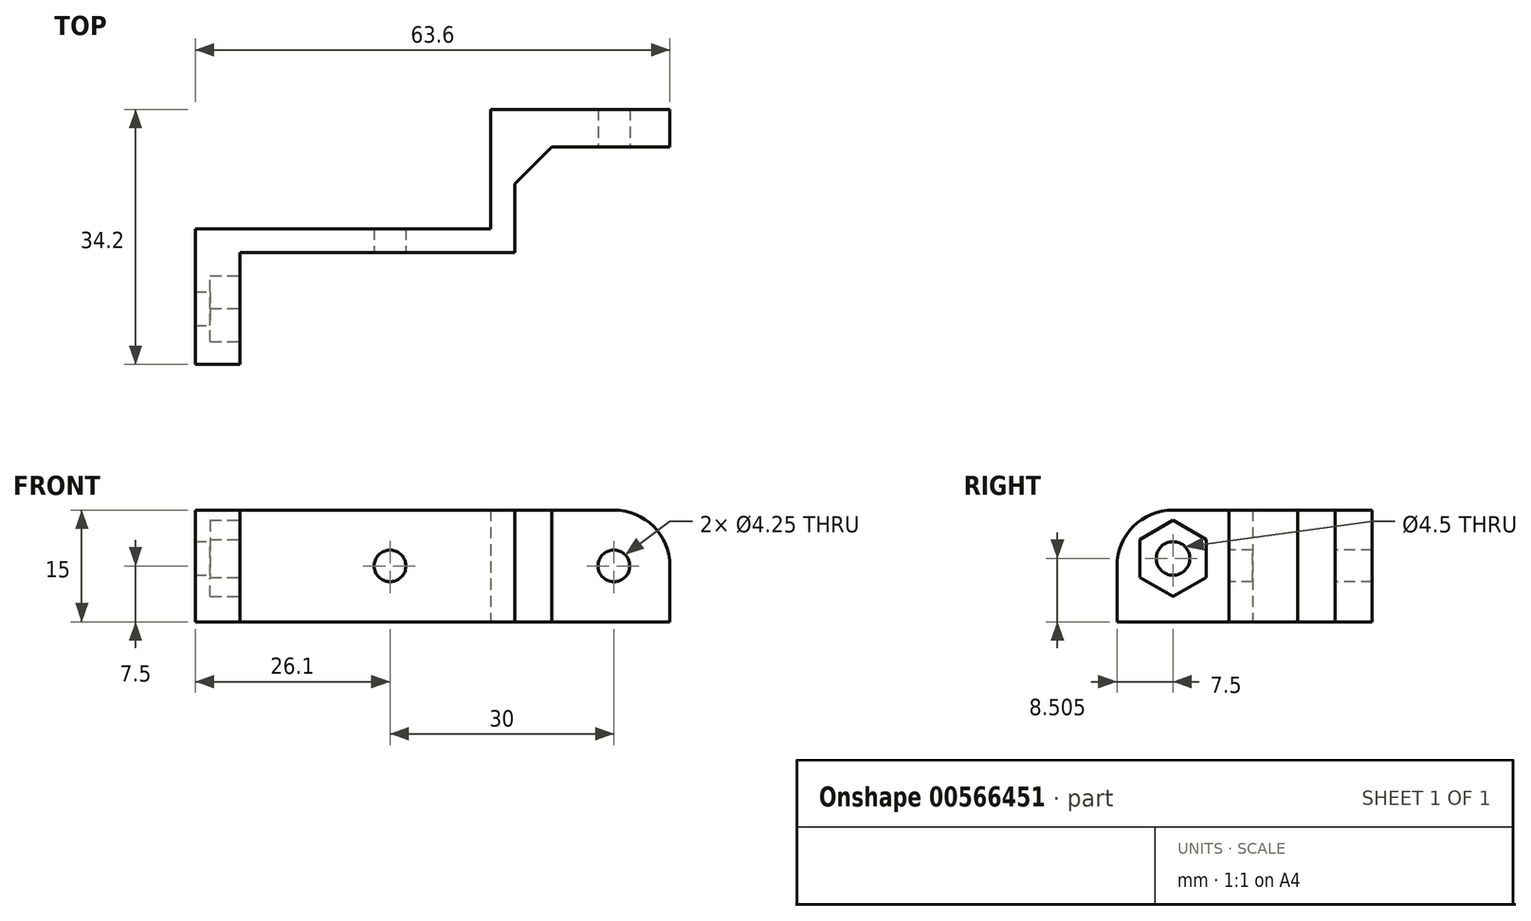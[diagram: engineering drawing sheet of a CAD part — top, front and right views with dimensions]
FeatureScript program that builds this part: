
annotation { "Feature Type Name" : "Feature", "Feature Type Description" : "" }
export const myFeature = defineFeature(function(context is Context, id is Id, definition is map)
    precondition{}
    {
        {
            var Q0;
            Q0=qCreatedBy(makeId("Top.planeOp"),FACE);
            var sketch = newSketch(context, id + "F0", { "sketchPlane" : qUnion([Q0])});
            skLineSegment(sketch, "E0", {"start": v(0, 0) * mm, "end": v(-16.7, 0) * mm});
            skLineSegment(sketch, "E1", {"start": v(-16.7, 0) * mm, "end": v(-16.7, 14.2) * mm, "construction": true});
            skLineSegment(sketch, "E2", {"start": v(-47.5, 14.2) * mm, "end": v(-47.5, 19.2) * mm, "construction": true});
            skLineSegment(sketch, "E3", {"start": v(-13.5, 19.2) * mm, "end": v(-13.5, 3.2) * mm, "construction": true});
            skLineSegment(sketch, "E4", {"start": v(-13.5, 3.2) * mm, "end": v(0, 3.2) * mm});
            skLineSegment(sketch, "E5.MirrorCS", {"start": v(47.5, 14.2) * mm, "end": v(47.5, 19.2) * mm, "construction": true});
            skLineSegment(sketch, "E6.MirrorCS", {"start": v(16.7, 14.2) * mm, "end": v(47.5, 14.2) * mm, "construction": true});
            skLineSegment(sketch, "E7.MirrorCS", {"start": v(47.5, 19.2) * mm, "end": v(13.5, 19.2) * mm, "construction": true});
            skLineSegment(sketch, "E8.MirrorCS", {"start": v(0, 0) * mm, "end": v(16.7, 0) * mm});
            skLineSegment(sketch, "E9.MirrorCS", {"start": v(13.5, 3.2) * mm, "end": v(0, 3.2) * mm});
            skLineSegment(sketch, "E10.MirrorCS", {"start": v(16.7, 0) * mm, "end": v(16.7, 14.2) * mm});
            skLineSegment(sketch, "E11.MirrorCS", {"start": v(13.5, 19.2) * mm, "end": v(13.5, 3.2) * mm});
            skLineSegment(sketch, "E12", {"start": v(13.5, 19.2) * mm, "end": v(37.5, 19.2) * mm});
            skLineSegment(sketch, "E13", {"start": v(37.5, 19.2) * mm, "end": v(37.5, 14.2) * mm});
            skLineSegment(sketch, "E14", {"start": v(37.5, 14.2) * mm, "end": v(16.7, 14.2) * mm});
            skLineSegment(sketch, "E15", {"start": v(-26.1, 3.2) * mm, "end": v(-13.5, 3.2) * mm});
            skPoint(sketch, "E16.orphan", {"position": v(-20.5, 0) * mm});
            skLineSegment(sketch, "E17", {"start": v(-26.1, 3.2) * mm, "end": v(-26.1, -15) * mm});
            skLineSegment(sketch, "E18", {"start": v(-26.1, -15) * mm, "end": v(-20.1, -15) * mm});
            skLineSegment(sketch, "E19", {"start": v(-20.1, -15) * mm, "end": v(-20.1, 0) * mm});
            skLineSegment(sketch, "E20", {"start": v(-20.1, 0) * mm, "end": v(-16.7, 0) * mm});
            skSolve(sketch);
        }
        {
            var Q0;
            Q0=qSketchRegion(id+"F0",true);
            extrude(context, id + "F1", {"entities" : qUnion([Q0]), "depth" : 15 * mm, "offsetDistance" : 25 * mm});
        }
        {
            var Q0;
            Q0=makeQuery(id+"F1.opExtrude","SWEPT_FACE",FACE,{"disambiguationData":[OSD([sQuery(id+"F0.wireOp",EDGE,"E0"),sQuery(id+"F0.wireOp",EDGE,"E8.MirrorCS")])]});
            var sketch = newSketch(context, id + "F2", { "sketchPlane" : qUnion([Q0])});
            skCircle(sketch, "E21", {"center": v(0, 7.5) * mm, "radius": 2.12 * mm});
            skCircle(sketch, "E22", {"center": v(30, 7.5) * mm, "radius": 2.12 * mm});
            skSolve(sketch);
        }
        {
            var Q0;
            Q0=qSketchRegion(id+"F2",true);
            extrude(context, id + "F3", {"entities" : qUnion([Q0]), "operationType" : NewBodyOperationType.REMOVE, "oppositeDirection" : true, "depth" : 25 * mm, "offsetDistance" : 25 * mm});
        }
        {
            var Q0;
            Q0=makeQuery(id+"F1.opExtrude","SWEPT_EDGE",EDGE,{"disambiguationData":[OSD([sQuery(id+"F0.wireOp",EDGE,"kh5gqzDc-j2E5-55WK-DO6c-lwDGbMsBLs6B"),sQuery(id+"F0.wireOp",EDGE,"1KyJL7GZ-X7l8-gq30-QFCO-WSz9YLhEHFXo")])]});
            var Q1;
            Q1=makeQuery(id+"F1.opExtrude","SWEPT_EDGE",EDGE,{"disambiguationData":[OSD([sQuery(id+"F0.wireOp",EDGE,"E10.MirrorCS"),sQuery(id+"F0.wireOp",EDGE,"E14")])]});
            chamfer(context, id + "F4", {"entities" : qUnion([Q0, Q1]), "width" : 5 * mm, "tangentPropagation" : true});
        }
        {
            var Q0;
            Q0=makeQuery(id+"F1.opExtrude","CAP_EDGE",EDGE,{"disambiguationData":[OSD([sQuery(id+"F0.wireOp",EDGE,"E2")])],"isStart":false});
            var Q1;
            Q1=makeQuery(id+"F1.opExtrude","CAP_EDGE",EDGE,{"disambiguationData":[OSD([sQuery(id+"F0.wireOp",EDGE,"E13")])],"isStart":false});
            var Q2;
            Q2=makeQuery(id+"F1.opExtrude","CAP_EDGE",EDGE,{"disambiguationData":[OSD([sQuery(id+"F0.wireOp",EDGE,"E18")])],"isStart":false});
            fillet(context, id + "F5", {"entities" : qUnion([Q0, Q1, Q2]), "radius" : 7.5 * mm, "tangentPropagation" : true, "allowEdgeOverflow" : false});
        }
        {
            var Q0;
            Q0=makeQuery(id+"F1.opExtrude","SWEPT_FACE",FACE,{"disambiguationData":[OSD([sQuery(id+"F0.wireOp",EDGE,"E19")])]});
            var sketch = newSketch(context, id + "F6", { "sketchPlane" : qUnion([Q0])});
            skCircle(sketch, "E23", {"center": v(-7.5, 8.5) * mm, "radius": 2.25 * mm});
            skSolve(sketch);
        }
        {
            var Q0;
            Q0=qSketchRegion(id+"F6",true);
            extrude(context, id + "F7", {"entities" : qUnion([Q0]), "operationType" : NewBodyOperationType.REMOVE, "oppositeDirection" : true, "depth" : 25 * mm, "offsetDistance" : 25 * mm});
        }
        {
            var Q0;
            Q0=makeQuery(id+"F1.opExtrude","SWEPT_FACE",FACE,{"disambiguationData":[OSD([sQuery(id+"F0.wireOp",EDGE,"E19")])]});
            var sketch = newSketch(context, id + "F8", { "sketchPlane" : qUnion([Q0])});
            skCircle(sketch, "E24.cCircle", {"center": v(-7.5, 8.5) * mm, "radius": 4.42 * mm, "construction": true});
            skLineSegment(sketch, "E24.0", {"start": v(-3.08, 11.06) * mm, "end": v(-3.08, 5.95) * mm});
            skLineSegment(sketch, "E24.1", {"start": v(-3.08, 5.95) * mm, "end": v(-7.5, 3.4) * mm});
            skLineSegment(sketch, "E24.2", {"start": v(-7.5, 3.4) * mm, "end": v(-11.92, 5.95) * mm});
            skLineSegment(sketch, "E24.3", {"start": v(-11.92, 5.95) * mm, "end": v(-11.92, 11.06) * mm});
            skLineSegment(sketch, "E24.4", {"start": v(-11.92, 11.06) * mm, "end": v(-7.5, 13.61) * mm});
            skLineSegment(sketch, "E24.5", {"start": v(-7.5, 13.61) * mm, "end": v(-3.08, 11.06) * mm});
            skPoint(sketch, "E24.0.midPoint", {"position": v(-3.08, 8.5) * mm});
            skSolve(sketch);
        }
        {
            var Q0;
            Q0=qSketchRegion(id+"F8",true);
            extrude(context, id + "F9", {"entities" : qUnion([Q0]), "operationType" : NewBodyOperationType.REMOVE, "oppositeDirection" : true, "depth" : 4 * mm, "offsetDistance" : 25 * mm});
        }
    });
